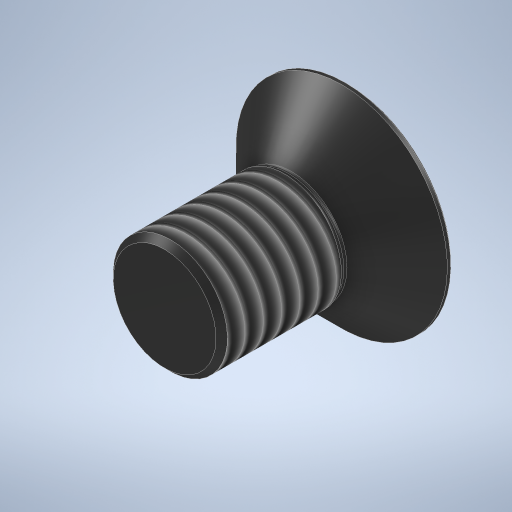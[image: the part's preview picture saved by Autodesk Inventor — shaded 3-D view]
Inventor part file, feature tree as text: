
AUTODESK INVENTOR PART (.ipt)
format: ipt  version: 2024 (Build 280153000, 153)  size: 384,000 bytes
history: native  units: mm
features: chamfer x3, sketch x2, revolve x1, fillet x1, thread x1, hole x1, extrude x1
ambient origin geometry x8: Origin, YZ Plane, XZ Plane, XY Plane, X Axis, Y Axis, Z Axis, Center Point
bodies: Solid2 (feature_tree)
feature tree (10):
  revolve  "Revolution1"  Angle=45.0deg
  fillet  "Fillet1"  Radius=3.0mm
  thread  "Thread1"  [1 undecoded]
  chamfer  "Chamfer1"  Distance=3.94mm
  sketch  "Sketch2"  dims[d6=5.239mm d7=0.0mm d8=0.1mm d9=2.0mm d10=45.0deg d11=3.75mm d15=0.5mm d16=0.8mm d17=45.0deg d18=3.0mm d19=0.0mm d20=0.25mm d21=2.0mm d22=45.0deg]
  hole  "Hole1"  [1 undecoded]
  chamfer  "Chamfer2"  Distance=1.66mm
  extrude  "Extrusion4"  Depth=2.5mm
  chamfer  "Chamfer3"  Distance=4.625mm
  sketch  "Sketch3"  dims[d23=2.5mm d24=6.0mm d25=4.0mm d26=2.0mm d27=90.0deg d28=2.5mm d29=150.0deg d30=3.94mm d31=0.66mm d32=1.66mm d33=2.5mm d37=4.625mm d38=2.5mm d39=8.0mm d40=0.25mm d41=45.0deg d42=0.1mm d43=90.0deg d44=0.25mm d45=1.0mm d46=1.0mm d47=1.0mm d48=0.15mm d49=0.25mm d50=0.375mm d51=14.3117mm d52=0.75mm d53=20.594885mm d54=0.0625mm d55=0.75mm d56=0.375mm]
note: 2 required parameter values undecoded (feature->parameter linkage not recoverable at this tier; creation-order binding heuristic only, values carry confidence <= 0.55)
